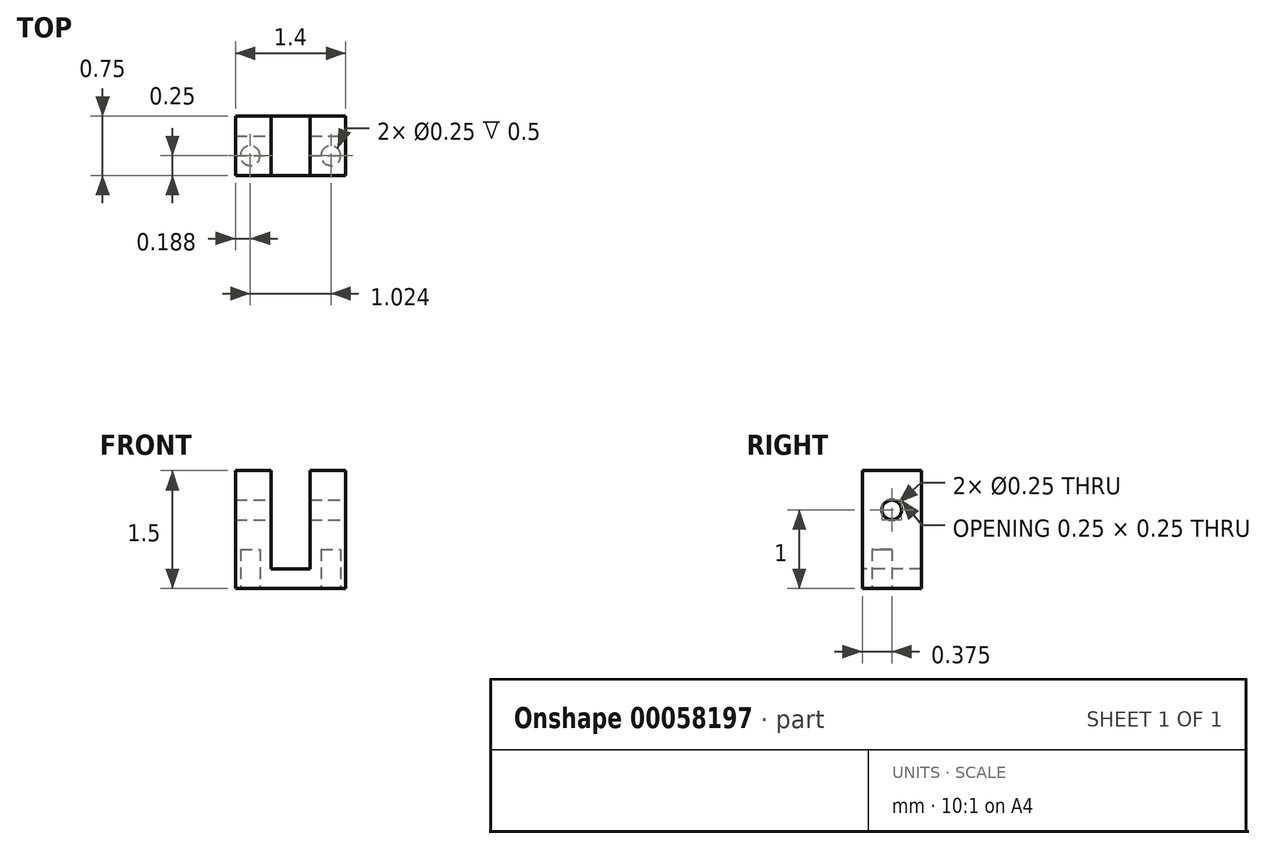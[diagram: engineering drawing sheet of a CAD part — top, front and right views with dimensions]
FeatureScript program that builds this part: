
annotation { "Feature Type Name" : "Feature", "Feature Type Description" : "" }
export const myFeature = defineFeature(function(context is Context, id is Id, definition is map)
    precondition{}
    {
        {
            var Q0;
            Q0=qCreatedBy(makeId("Front.planeOp"),FACE);
            var sketch = newSketch(context, id + "F0", { "sketchPlane" : qUnion([Q0])});
            skLineSegment(sketch, "E0.bottom", {"start": v(0, 0) * mm, "end": v(1.4, 0) * mm});
            skLineSegment(sketch, "E0.top", {"start": v(0, -1.5) * mm, "end": v(1.4, -1.5) * mm});
            skLineSegment(sketch, "E0.left", {"start": v(0, 0) * mm, "end": v(0, -1.5) * mm});
            skLineSegment(sketch, "E0.right", {"start": v(1.4, 0) * mm, "end": v(1.4, -1.5) * mm});
            skSolve(sketch);
        }
        {
            var Q0;
            Q0 = qSketchRegion(id + "F0", true);
            var Q1;
            Q1=makeQuery(id+"F0.imprint","IMPRINT",FACE,{"disambiguationData":[TD([[makeQuery(id+"F0.imprint","IMPRINT",EDGE,{"derivedFrom":sQuery(id+"F0.wireOp",EDGE,"E0.bottom")}),-1.0]])]});
            extrude(context, id + "F1", {"entities" : qUnion([Q0, Q1]), "depth" : 0.75 * mm});
        }
        {
            var Q0;
            Q0=makeQuery(id+"F1.opExtrude","SWEPT_FACE",FACE,{"disambiguationData":[OSD([sQuery(id+"F0.wireOp",EDGE,"E0.right")])]});
            var sketch = newSketch(context, id + "F2", { "sketchPlane" : qUnion([Q0])});
            skLineSegment(sketch, "E1", {"start": v(0, 0) * mm, "end": v(-0.38, 0) * mm});
            skCircle(sketch, "E2", {"center": v(-0.38, -0.5) * mm, "radius": 0.12 * mm});
            skLineSegment(sketch, "E3", {"start": v(-0.38, -0.5) * mm, "end": v(-0.38, -1.5) * mm});
            skSolve(sketch);
        }
        {
            var Q0;
            Q0 = qSketchRegion(id + "F2", true);
            extrude(context, id + "F3", {"entities" : qUnion([Q0]), "operationType" : NewBodyOperationType.REMOVE, "oppositeDirection" : true, "depth" : 25 * mm});
        }
        {
            var Q0;
            Q0=makeQuery(id+"F1.opExtrude","CAP_FACE",FACE,{"disambiguationData":[OSD([sQuery(id+"F0.wireOp",EDGE,"E0.bottom"),sQuery(id+"F0.wireOp",EDGE,"E0.top"),sQuery(id+"F0.wireOp",EDGE,"E0.left"),sQuery(id+"F0.wireOp",EDGE,"E0.right")])],"isStart":false});
            var sketch = newSketch(context, id + "F4", { "sketchPlane" : qUnion([Q0])});
            skLineSegment(sketch, "E4", {"start": v(1.4, 0) * mm, "end": v(0.95, 0) * mm});
            skLineSegment(sketch, "E5", {"start": v(0.95, 0) * mm, "end": v(0.95, -1.25) * mm});
            skLineSegment(sketch, "E6", {"start": v(0, 0) * mm, "end": v(0.45, 0) * mm});
            skLineSegment(sketch, "E7", {"start": v(0.45, 0) * mm, "end": v(0.45, -1.25) * mm});
            skLineSegment(sketch, "E8", {"start": v(0.45, -1.25) * mm, "end": v(0.95, -1.25) * mm});
            skSolve(sketch);
        }
        {
            var Q0;
            Q0 = qSketchRegion(id + "F4", true);
            var Q1;
            {var subQ0=sQuery(id+"F4.wireOp",EDGE,"E5");Q1=makeQuery(id+"F4.imprint","IMPRINT",FACE,{"disambiguationData":[TD([[makeQuery(id+"F4.imprint","IMPRINT",EDGE,{"derivedFrom":subQ0}),-1.0]])]});}
            extrude(context, id + "F5", {"entities" : qUnion([Q0, Q1]), "operationType" : NewBodyOperationType.REMOVE, "oppositeDirection" : true, "depth" : 25 * mm});
        }
        {
            var Q0;
            Q0=makeQuery(id+"F1.opExtrude","SWEPT_FACE",FACE,{"disambiguationData":[OSD([sQuery(id+"F0.wireOp",EDGE,"E0.top")])]});
            var sketch = newSketch(context, id + "F6", { "sketchPlane" : qUnion([Q0])});
            skLineSegment(sketch, "E9", {"start": v(1.4, 0.75) * mm, "end": v(1.21, 0.75) * mm});
            skLineSegment(sketch, "E10", {"start": v(0, 0.75) * mm, "end": v(0.19, 0.75) * mm});
            skLineSegment(sketch, "E11", {"start": v(0, 0.75) * mm, "end": v(0, 0.5) * mm});
            skLineSegment(sketch, "E12", {"start": v(1.4, 0.75) * mm, "end": v(1.4, 0.5) * mm});
            skCircle(sketch, "E13", {"center": v(0.19, 0.5) * mm, "radius": 0.12 * mm});
            skCircle(sketch, "E14", {"center": v(1.21, 0.5) * mm, "radius": 0.12 * mm});
            skSolve(sketch);
        }
        {
            var Q0;
            Q0 = qSketchRegion(id + "F6", true);
            var Q1;
            Q1=makeQuery(id+"F6.imprint","IMPRINT",FACE,{"disambiguationData":[TD([[makeQuery(id+"F6.imprint","IMPRINT",EDGE,{"derivedFrom":sQuery(id+"F6.wireOp",EDGE,"E13")}),1.0]])]});
            extrude(context, id + "F7", {"entities" : qUnion([Q0, Q1]), "operationType" : NewBodyOperationType.REMOVE, "oppositeDirection" : true, "depth" : 0.5 * mm});
        }
    });
